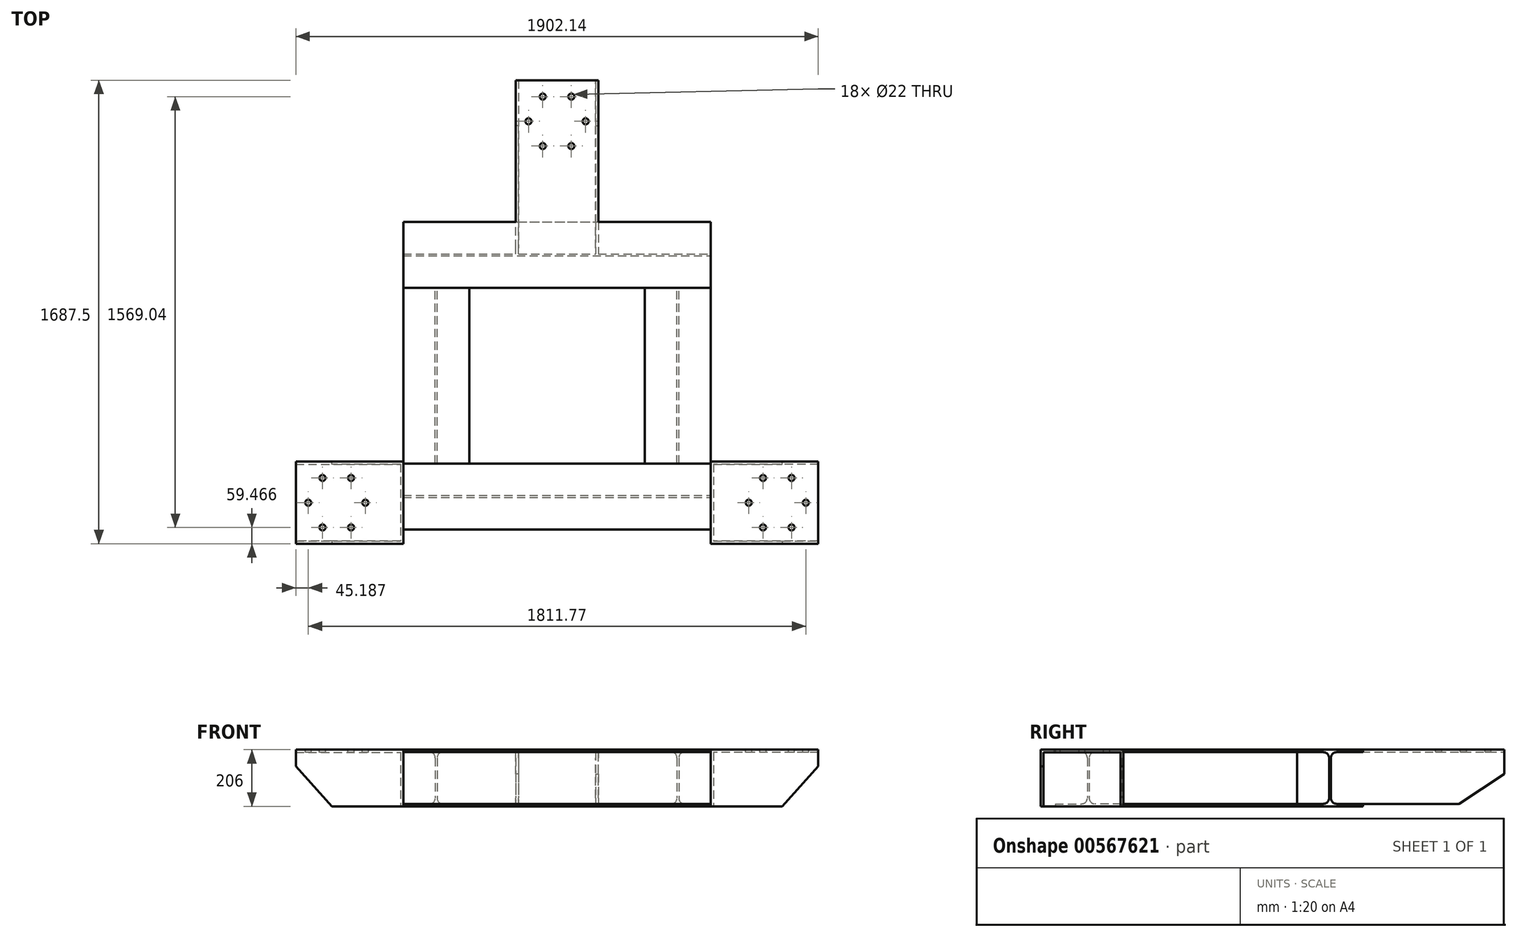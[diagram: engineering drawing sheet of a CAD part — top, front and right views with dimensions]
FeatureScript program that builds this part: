
annotation { "Feature Type Name" : "Feature", "Feature Type Description" : "" }
export const myFeature = defineFeature(function(context is Context, id is Id, definition is map)
    precondition{}
    {
        {
            var Q0;
            Q0=qCreatedBy(makeId("Top.planeOp"),FACE);
            var sketch = newSketch(context, id + "F0", { "sketchPlane" : qUnion([Q0])});
            skLineSegment(sketch, "E0.bottom", {"start": v(560, -560) * mm, "end": v(-560, -560) * mm});
            skLineSegment(sketch, "E0.top", {"start": v(560, 560) * mm, "end": v(-560, 560) * mm});
            skLineSegment(sketch, "E0.left", {"start": v(560, -560) * mm, "end": v(560, 560) * mm});
            skLineSegment(sketch, "E0.right", {"start": v(-560, -560) * mm, "end": v(-560, 560) * mm});
            skPoint(sketch, "E0.middle", {"position": v(0, 0) * mm});
            skSolve(sketch);
        }
        {
            var Q0;
            Q0=sQuery(id+"F0.wireOp",VERTEX,"E0.bottom.start");
            var Q1;
            Q1=sQuery(id+"F0.wireOp",EDGE,"E0.bottom");
            cPlane(context, id + "F1", {"entities" : qUnion([Q0, Q1]), "cplaneType" : CPlaneType.LINE_POINT, "offset" : 25 * mm, "width" : 150 * mm, "height" : 150 * mm});
        }
        {
            var Q0;
            Q0=qCreatedBy(id+"F1.planeOp",FACE);
            var sketch = newSketch(context, id + "F2", { "sketchPlane" : qUnion([Q0])});
            skLineSegment(sketch, "E1.bottom", {"start": v(560, 0) * mm, "end": v(320, 0) * mm});
            skLineSegment(sketch, "E1.top", {"start": v(560, -206) * mm, "end": v(320, -206) * mm});
            skLineSegment(sketch, "E1.left", {"start": v(560, 0) * mm, "end": v(560, -9) * mm});
            skLineSegment(sketch, "E1.right", {"start": v(320, 0) * mm, "end": v(320, -9) * mm});
            skLineSegment(sketch, "E2.bottom", {"start": v(560, -9) * mm, "end": v(464.25, -9) * mm});
            skLineSegment(sketch, "E2.top", {"start": v(560, -197) * mm, "end": v(464.25, -197) * mm});
            skLineSegment(sketch, "E2.right", {"start": v(443.25, -30) * mm, "end": v(443.25, -176) * mm});
            skLineSegment(sketch, "E3.bottom", {"start": v(320, -9) * mm, "end": v(415.75, -9) * mm});
            skLineSegment(sketch, "E3.top", {"start": v(320, -197) * mm, "end": v(415.75, -197) * mm});
            skLineSegment(sketch, "E3.right", {"start": v(436.75, -30) * mm, "end": v(436.75, -176) * mm});
            skLineSegment(sketch, "E4.trimOffspring", {"start": v(320, -197) * mm, "end": v(320, -206) * mm});
            skLineSegment(sketch, "E5.trimOffspring", {"start": v(560, -197) * mm, "end": v(560, -206) * mm});
            skPoint(sketch, "E6.visualSharp", {"position": v(443.25, -9) * mm});
            skArc(sketch, "E6.filletArc", {"start": v(464.25, -9) * mm, "mid": v(449.4, -15.15) * mm, "end": v(443.25, -30) * mm});
            skPoint(sketch, "E7.visualSharp", {"position": v(436.75, -9) * mm});
            skArc(sketch, "E7.filletArc", {"start": v(436.75, -30) * mm, "mid": v(430.6, -15.15) * mm, "end": v(415.75, -9) * mm});
            skPoint(sketch, "E8.visualSharp", {"position": v(436.75, -197) * mm});
            skArc(sketch, "E8.filletArc", {"start": v(415.75, -197) * mm, "mid": v(430.6, -190.85) * mm, "end": v(436.75, -176) * mm});
            skPoint(sketch, "E9.visualSharp", {"position": v(443.25, -197) * mm});
            skArc(sketch, "E9.filletArc", {"start": v(443.25, -176) * mm, "mid": v(449.4, -190.85) * mm, "end": v(464.25, -197) * mm});
            skLineSegment(sketch, "E10", {"start": v(0, 0) * mm, "end": v(0, -326.36) * mm});
            skLineSegment(sketch, "E11.MirrorCS", {"start": v(-560, 0) * mm, "end": v(-560, -9) * mm});
            skArc(sketch, "E12.MirrorCS", {"start": v(-464.25, -9) * mm, "mid": v(-449.4, -15.15) * mm, "end": v(-443.25, -30) * mm});
            skArc(sketch, "E13.MirrorCS", {"start": v(-415.75, -197) * mm, "mid": v(-430.6, -190.85) * mm, "end": v(-436.75, -176) * mm});
            skArc(sketch, "E14.MirrorCS", {"start": v(-443.25, -176) * mm, "mid": v(-449.4, -190.85) * mm, "end": v(-464.25, -197) * mm});
            skLineSegment(sketch, "E15.MirrorCS", {"start": v(-320, -197) * mm, "end": v(-320, -206) * mm});
            skArc(sketch, "E16.MirrorCS", {"start": v(-436.75, -30) * mm, "mid": v(-430.6, -15.15) * mm, "end": v(-415.75, -9) * mm});
            skLineSegment(sketch, "E17.MirrorCS", {"start": v(-560, -197) * mm, "end": v(-560, -206) * mm});
            skLineSegment(sketch, "E18.MirrorCS", {"start": v(-320, 0) * mm, "end": v(-320, -9) * mm});
            skLineSegment(sketch, "E19.MirrorCS", {"start": v(-320, -197) * mm, "end": v(-415.75, -197) * mm});
            skLineSegment(sketch, "E20.MirrorCS", {"start": v(-320, -9) * mm, "end": v(-415.75, -9) * mm});
            skLineSegment(sketch, "E21.MirrorCS", {"start": v(-443.25, -30) * mm, "end": v(-443.25, -176) * mm});
            skPoint(sketch, "E22.MirrorP", {"position": v(-436.75, -197) * mm});
            skLineSegment(sketch, "E23.MirrorCS", {"start": v(-560, 0) * mm, "end": v(-320, 0) * mm});
            skPoint(sketch, "E24.MirrorP", {"position": v(-443.25, -197) * mm});
            skPoint(sketch, "E25.MirrorP", {"position": v(-436.75, -9) * mm});
            skLineSegment(sketch, "E26.MirrorCS", {"start": v(-560, -206) * mm, "end": v(-320, -206) * mm});
            skPoint(sketch, "E27.MirrorP", {"position": v(-443.25, -9) * mm});
            skLineSegment(sketch, "E28.MirrorCS", {"start": v(-560, -9) * mm, "end": v(-464.25, -9) * mm});
            skLineSegment(sketch, "E29.MirrorCS", {"start": v(-560, -197) * mm, "end": v(-464.25, -197) * mm});
            skLineSegment(sketch, "E30.MirrorCS", {"start": v(-436.75, -30) * mm, "end": v(-436.75, -176) * mm});
            skSolve(sketch);
        }
        {
            var Q0;
            Q0 = qSketchRegion(id + "F2", true);
            extrude(context, id + "F3", {"entities" : qUnion([Q0]), "depth" : 1120 * mm, "offsetDistance" : 25 * mm});
        }
        {
            var Q0;
            Q0=makeQuery(id+"F3.opExtrude","SWEPT_FACE",FACE,{"disambiguationData":[OSD([sQuery(id+"F2.wireOp",EDGE,"E18.MirrorCS")])]});
            var sketch = newSketch(context, id + "F4", { "sketchPlane" : qUnion([Q0])});
            skLineSegment(sketch, "E31.MirrorCS", {"start": v(-560, 0) * mm, "end": v(-560, -9) * mm});
            skArc(sketch, "E32.MirrorCS", {"start": v(-464.25, -9) * mm, "mid": v(-449.4, -15.15) * mm, "end": v(-443.25, -30) * mm});
            skArc(sketch, "E33.MirrorCS", {"start": v(-415.75, -197) * mm, "mid": v(-430.6, -190.85) * mm, "end": v(-436.75, -176) * mm});
            skArc(sketch, "E34.MirrorCS", {"start": v(-443.25, -176) * mm, "mid": v(-449.4, -190.85) * mm, "end": v(-464.25, -197) * mm});
            skLineSegment(sketch, "E35.MirrorCS", {"start": v(-320, -197) * mm, "end": v(-320, -206) * mm});
            skArc(sketch, "E36.MirrorCS", {"start": v(-436.75, -30) * mm, "mid": v(-430.6, -15.15) * mm, "end": v(-415.75, -9) * mm});
            skLineSegment(sketch, "E37.MirrorCS", {"start": v(-560, -197) * mm, "end": v(-560, -206) * mm});
            skLineSegment(sketch, "E38.MirrorCS", {"start": v(-320, 0) * mm, "end": v(-320, -9) * mm});
            skLineSegment(sketch, "E39.MirrorCS", {"start": v(-320, -197) * mm, "end": v(-415.75, -197) * mm});
            skLineSegment(sketch, "E40.MirrorCS", {"start": v(-320, -9) * mm, "end": v(-415.75, -9) * mm});
            skLineSegment(sketch, "E41.MirrorCS", {"start": v(-443.25, -30) * mm, "end": v(-443.25, -176) * mm});
            skPoint(sketch, "E42.MirrorP", {"position": v(-436.75, -197) * mm});
            skLineSegment(sketch, "E43.MirrorCS", {"start": v(-560, 0) * mm, "end": v(-320, 0) * mm});
            skPoint(sketch, "E44.MirrorP", {"position": v(-443.25, -197) * mm});
            skPoint(sketch, "E45.MirrorP", {"position": v(-436.75, -9) * mm});
            skLineSegment(sketch, "E46.MirrorCS", {"start": v(-560, -206) * mm, "end": v(-320, -206) * mm});
            skPoint(sketch, "E47.MirrorP", {"position": v(-443.25, -9) * mm});
            skLineSegment(sketch, "E48.MirrorCS", {"start": v(-560, -9) * mm, "end": v(-464.25, -9) * mm});
            skLineSegment(sketch, "E49.MirrorCS", {"start": v(-560, -197) * mm, "end": v(-464.25, -197) * mm});
            skLineSegment(sketch, "E50.MirrorCS", {"start": v(-436.75, -30) * mm, "end": v(-436.75, -176) * mm});
            skPoint(sketch, "E51.endSnap0", {"position": v(0, -9) * mm});
            skLineSegment(sketch, "E52.MirrorCS", {"start": v(560, -197) * mm, "end": v(560, -206) * mm});
            skArc(sketch, "E53.MirrorCS", {"start": v(415.75, -197) * mm, "mid": v(430.6, -190.85) * mm, "end": v(436.75, -176) * mm});
            skLineSegment(sketch, "E54.MirrorCS", {"start": v(560, 0) * mm, "end": v(560, -9) * mm});
            skArc(sketch, "E55.MirrorCS", {"start": v(443.25, -176) * mm, "mid": v(449.4, -190.85) * mm, "end": v(464.25, -197) * mm});
            skArc(sketch, "E56.MirrorCS", {"start": v(436.75, -30) * mm, "mid": v(430.6, -15.15) * mm, "end": v(415.75, -9) * mm});
            skArc(sketch, "E57.MirrorCS", {"start": v(464.25, -9) * mm, "mid": v(449.4, -15.15) * mm, "end": v(443.25, -30) * mm});
            skLineSegment(sketch, "E58.MirrorCS", {"start": v(320, -197) * mm, "end": v(320, -206) * mm});
            skPoint(sketch, "E59.MirrorP", {"position": v(436.75, -9) * mm});
            skLineSegment(sketch, "E60.MirrorCS", {"start": v(320, -197) * mm, "end": v(415.75, -197) * mm});
            skLineSegment(sketch, "E61.MirrorCS", {"start": v(443.25, -30) * mm, "end": v(443.25, -176) * mm});
            skLineSegment(sketch, "E62.MirrorCS", {"start": v(560, -197) * mm, "end": v(464.25, -197) * mm});
            skLineSegment(sketch, "E63.MirrorCS", {"start": v(560, -9) * mm, "end": v(464.25, -9) * mm});
            skLineSegment(sketch, "E64.MirrorCS", {"start": v(436.75, -30) * mm, "end": v(436.75, -176) * mm});
            skLineSegment(sketch, "E65.MirrorCS", {"start": v(560, -206) * mm, "end": v(320, -206) * mm});
            skPoint(sketch, "E66.MirrorP", {"position": v(443.25, -9) * mm});
            skPoint(sketch, "E67.MirrorP", {"position": v(443.25, -197) * mm});
            skPoint(sketch, "E68.MirrorP", {"position": v(436.75, -197) * mm});
            skLineSegment(sketch, "E69.MirrorCS", {"start": v(320, -9) * mm, "end": v(415.75, -9) * mm});
            skLineSegment(sketch, "E70.MirrorCS", {"start": v(560, 0) * mm, "end": v(320, 0) * mm});
            skLineSegment(sketch, "E71", {"start": v(320, 0) * mm, "end": v(320, -9) * mm});
            skSolve(sketch);
        }
        {
            var Q0;
            Q0 = qSketchRegion(id + "F4", true);
            var Q1;
            Q1=makeQuery(id+"F3.opExtrude","SWEPT_FACE",FACE,{"disambiguationData":[OSD([sQuery(id+"F2.wireOp",EDGE,"E4.trimOffspring")])]});
            extrude(context, id + "F5", {"entities" : qUnion([Q0]), "endBound" : BoundingType.UP_TO_SURFACE, "depth" : 25 * mm, "endBoundEntityFace" : qUnion([Q1]), "offsetDistance" : 25 * mm});
        }
        {
            var Q0;
            Q0=makeQuery(id+"F0.imprint","IMPRINT",FACE,{"disambiguationData":[TD([[makeQuery(id+"F0.imprint","IMPRINT",EDGE,{"derivedFrom":sQuery(id+"F0.wireOp",EDGE,"E0.bottom")}),-1.0]])]});
            var sketch = newSketch(context, id + "F6", { "sketchPlane" : qUnion([Q0])});
            skLineSegment(sketch, "E72", {"start": v(-801.07, -462.5) * mm, "end": v(801.07, -462.5) * mm});
            skLineSegment(sketch, "E73", {"start": v(0, 925) * mm, "end": v(-801.07, -462.5) * mm});
            skLineSegment(sketch, "E74", {"start": v(0, 925) * mm, "end": v(801.07, -462.5) * mm});
            skLineSegment(sketch, "E75", {"start": v(-801.07, -462.5) * mm, "end": v(400.54, 231.25) * mm});
            skLineSegment(sketch, "E76", {"start": v(801.07, -462.5) * mm, "end": v(-400.54, 231.25) * mm});
            skPoint(sketch, "E77", {"position": v(0, 0) * mm});
            skSolve(sketch);
        }
        {
            var Q0;
            Q0=makeQuery(id+"F0.imprint","IMPRINT",FACE,{"disambiguationData":[TD([[makeQuery(id+"F0.imprint","IMPRINT",EDGE,{"derivedFrom":sQuery(id+"F0.wireOp",EDGE,"E0.bottom")}),-1.0]])]});
            var sketch = newSketch(context, id + "F7", { "sketchPlane" : qUnion([Q0])});
            skLineSegment(sketch, "E78.0", {"start": v(560, 560) * mm, "end": v(-560, 560) * mm, "construction": true});
            skLineSegment(sketch, "E79.bottom", {"start": v(-150, 560) * mm, "end": v(150, 560) * mm});
            skLineSegment(sketch, "E79.left", {"start": v(-150, 560) * mm, "end": v(-150, 925) * mm});
            skLineSegment(sketch, "E79.right", {"start": v(150, 560) * mm, "end": v(150, 925) * mm});
            skLineSegment(sketch, "E80", {"start": v(-150, 925) * mm, "end": v(-150, 1075) * mm});
            skLineSegment(sketch, "E81", {"start": v(-150, 1075) * mm, "end": v(150, 1075) * mm});
            skLineSegment(sketch, "E82", {"start": v(150, 925) * mm, "end": v(150, 1075) * mm});
            skSolve(sketch);
        }
        {
            var Q0;
            Q0=makeQuery(id+"F7.imprint","IMPRINT",FACE,{"disambiguationData":[TD([[makeQuery(id+"F7.imprint","IMPRINT",EDGE,{"derivedFrom":sQuery(id+"F7.wireOp",EDGE,"E79.bottom")}),-1.0]])]});
            extrude(context, id + "F8", {"entities" : qUnion([Q0]), "operationType" : NewBodyOperationType.ADD, "oppositeDirection" : true, "depth" : 9 * mm, "offsetDistance" : 25 * mm});
        }
        {
            var Q0;
            Q0=makeQuery(id+"F8.opExtrude","SWEPT_FACE",FACE,{"disambiguationData":[OSD([sQuery(id+"F7.wireOp",EDGE,"E79.left"),sQuery(id+"F7.wireOp",EDGE,"E80")])]});
            var sketch = newSketch(context, id + "F9", { "sketchPlane" : qUnion([Q0])});
            skLineSegment(sketch, "E83.0", {"start": v(-560, -9) * mm, "end": v(-464.25, -9) * mm});
            skArc(sketch, "E84.0", {"start": v(-464.25, -9) * mm, "mid": v(-449.4, -15.15) * mm, "end": v(-443.25, -30) * mm});
            skLineSegment(sketch, "E85.0", {"start": v(-443.25, -30) * mm, "end": v(-443.25, -176) * mm});
            skArc(sketch, "E86.0", {"start": v(-443.25, -176) * mm, "mid": v(-449.4, -190.85) * mm, "end": v(-464.25, -197) * mm});
            skLineSegment(sketch, "E87.0", {"start": v(-560, -197) * mm, "end": v(-464.25, -197) * mm});
            skLineSegment(sketch, "E88.0", {"start": v(-560, -9) * mm, "end": v(-560, -9) * mm});
            skLineSegment(sketch, "E89", {"start": v(-560, -197) * mm, "end": v(747.25, -197) * mm});
            skLineSegment(sketch, "E90", {"start": v(-560, -197) * mm, "end": v(-910, -197) * mm});
            skLineSegment(sketch, "E91", {"start": v(-1075, -9) * mm, "end": v(-1075, -89) * mm});
            skLineSegment(sketch, "E92", {"start": v(-1075, -89) * mm, "end": v(-910, -197) * mm});
            skLineSegment(sketch, "E93", {"start": v(-560, -9) * mm, "end": v(-1075, -9) * mm});
            skSolve(sketch);
        }
        {
            var Q0;
            Q0=makeQuery(id+"F9.imprint","IMPRINT",FACE,{"disambiguationData":[TD([[makeQuery(id+"F9.imprint","IMPRINT",EDGE,{"derivedFrom":sQuery(id+"F9.wireOp",EDGE,"E83.0")}),-1.0]])]});
            extrude(context, id + "F10", {"entities" : qUnion([Q0]), "operationType" : NewBodyOperationType.ADD, "oppositeDirection" : true, "depth" : 10 * mm, "offsetDistance" : 25 * mm});
        }
        {
            var Q0;
            Q0=makeQuery(id+"F8.opExtrude","SWEPT_FACE",FACE,{"disambiguationData":[OSD([sQuery(id+"F7.wireOp",EDGE,"E79.right"),sQuery(id+"F7.wireOp",EDGE,"E82")])]});
            var sketch = newSketch(context, id + "F11", { "sketchPlane" : qUnion([Q0])});
            skLineSegment(sketch, "E94.0.0", {"start": v(560, 0) * mm, "end": v(1075, 0) * mm});
            skLineSegment(sketch, "E94.0.1", {"start": v(1075, 0) * mm, "end": v(1075, -89) * mm});
            skLineSegment(sketch, "E94.0.2", {"start": v(1075, -89) * mm, "end": v(910, -197) * mm});
            skLineSegment(sketch, "E94.0.3", {"start": v(910, -197) * mm, "end": v(560, -197) * mm});
            skLineSegment(sketch, "E94.0.4", {"start": v(560, -197) * mm, "end": v(464.25, -197) * mm});
            skArc(sketch, "E94.0.5", {"start": v(464.25, -197) * mm, "mid": v(449.4, -190.85) * mm, "end": v(443.25, -176) * mm});
            skLineSegment(sketch, "E94.0.6", {"start": v(443.25, -176) * mm, "end": v(443.25, -30) * mm});
            skArc(sketch, "E94.0.7", {"start": v(443.25, -30) * mm, "mid": v(449.4, -15.15) * mm, "end": v(464.25, -9) * mm});
            skLineSegment(sketch, "E94.0.8", {"start": v(464.25, -9) * mm, "end": v(560, -9) * mm});
            skLineSegment(sketch, "E94.0.9", {"start": v(560, -9) * mm, "end": v(560, 0) * mm});
            skSolve(sketch);
        }
        {
            var Q0;
            {var subQ0=sQuery(id+"F11.wireOp",EDGE,"E94.0.2");Q0=makeQuery(id+"F11.imprint","IMPRINT",FACE,{"disambiguationData":[TD([[makeQuery(id+"F11.imprint","IMPRINT",EDGE,{"derivedFrom":subQ0}),-1.0]])]});}
            extrude(context, id + "F12", {"entities" : qUnion([Q0]), "operationType" : NewBodyOperationType.ADD, "oppositeDirection" : true, "depth" : 10 * mm, "offsetDistance" : 25 * mm});
        }
        {
            var Q0;
            Q0=makeQuery(id+"F3.opExtrude","CAP_FACE",FACE,{"disambiguationData":[OSD([sQuery(id+"F2.wireOp",EDGE,"E1.bottom"),sQuery(id+"F2.wireOp",EDGE,"E1.top"),sQuery(id+"F2.wireOp",EDGE,"E1.left"),sQuery(id+"F2.wireOp",EDGE,"E1.right"),sQuery(id+"F2.wireOp",EDGE,"E2.bottom"),sQuery(id+"F2.wireOp",EDGE,"E2.top"),sQuery(id+"F2.wireOp",EDGE,"E2.right"),sQuery(id+"F2.wireOp",EDGE,"E3.bottom"),sQuery(id+"F2.wireOp",EDGE,"E3.top"),sQuery(id+"F2.wireOp",EDGE,"E3.right"),sQuery(id+"F2.wireOp",EDGE,"E4.trimOffspring"),sQuery(id+"F2.wireOp",EDGE,"E5.trimOffspring"),sQuery(id+"F2.wireOp",EDGE,"E6.filletArc"),sQuery(id+"F2.wireOp",EDGE,"E7.filletArc"),sQuery(id+"F2.wireOp",EDGE,"E8.filletArc"),sQuery(id+"F2.wireOp",EDGE,"E9.filletArc")])],"isStart":false});
            var sketch = newSketch(context, id + "F13", { "sketchPlane" : qUnion([Q0])});
            skLineSegment(sketch, "E95.top", {"start": v(312.5, -206) * mm, "end": v(560, -206) * mm});
            skPoint(sketch, "E96.0", {"position": v(462.5, 0) * mm});
            skLineSegment(sketch, "E97", {"start": v(462.5, 0) * mm, "end": v(612.5, 0) * mm});
            skLineSegment(sketch, "E98", {"start": v(462.5, 0) * mm, "end": v(312.5, 0) * mm});
            skLineSegment(sketch, "E99", {"start": v(312.5, 0) * mm, "end": v(312.5, -206) * mm});
            skLineSegment(sketch, "E100", {"start": v(312.5, -206) * mm, "end": v(612.5, -206) * mm});
            skLineSegment(sketch, "E101", {"start": v(612.5, 0) * mm, "end": v(612.5, -206) * mm});
            skSolve(sketch);
        }
        {
            var Q0;
            {var subQ3=sQuery(id+"F13.wireOp",EDGE,"E99");Q0=makeQuery(id+"F13.imprint","IMPRINT",FACE,{"disambiguationData":[TD([[makeQuery(id+"F13.imprint","IMPRINT",EDGE,{"derivedFrom":subQ3}),1.0]])]});}
            var Q1;
            {var subQ2=makeQuery(id+"F3.opExtrude","CAP_EDGE",EDGE,{"disambiguationData":[OSD([sQuery(id+"F2.wireOp",EDGE,"E1.left")])],"isStart":false});Q1=makeQuery(id+"F13.imprint","IMPRINT",FACE,{"disambiguationData":[TD([[makeQuery(id+"F13.imprint","IMPRINT",EDGE,{"derivedFrom":subQ2}),-1.0]])]});}
            var Q2;
            {var subQ1=sQuery(id+"F13.wireOp",EDGE,"E101");Q2=makeQuery(id+"F13.imprint","IMPRINT",FACE,{"disambiguationData":[TD([[makeQuery(id+"F13.imprint","IMPRINT",EDGE,{"derivedFrom":subQ1}),-1.0]])]});}
            extrude(context, id + "F14", {"entities" : qUnion([Q0, Q1, Q2]), "depth" : 10 * mm, "offsetDistance" : 25 * mm});
        }
        {
            var Q0;
            Q0=makeQuery(id+"F14.opExtrude","CAP_FACE",FACE,{"disambiguationData":[OSD([sQuery(id+"F13.wireOp",EDGE,"E97"),sQuery(id+"F13.wireOp",EDGE,"E98"),sQuery(id+"F13.wireOp",EDGE,"E99"),sQuery(id+"F13.wireOp",EDGE,"E100"),sQuery(id+"F13.wireOp",EDGE,"E101")])],"isStart":false});
            var sketch = newSketch(context, id + "F15", { "sketchPlane" : qUnion([Q0])});
            skLineSegment(sketch, "E102.bottom", {"start": v(312.5, 0) * mm, "end": v(612.5, 0) * mm});
            skLineSegment(sketch, "E102.top", {"start": v(312.5, -10) * mm, "end": v(612.5, -10) * mm});
            skLineSegment(sketch, "E102.left", {"start": v(312.5, 0) * mm, "end": v(312.5, -10) * mm});
            skLineSegment(sketch, "E102.right", {"start": v(612.5, 0) * mm, "end": v(612.5, -10) * mm});
            skSolve(sketch);
        }
        {
            var Q0;
            Q0=makeQuery(id+"F15.imprint","IMPRINT",FACE,{"disambiguationData":[TD([[makeQuery(id+"F15.imprint","IMPRINT",EDGE,{"derivedFrom":sQuery(id+"F15.wireOp",EDGE,"E102.bottom")}),1.0]])]});
            extrude(context, id + "F16", {"entities" : qUnion([Q0]), "operationType" : NewBodyOperationType.ADD, "depth" : 381.07 * mm, "offsetDistance" : 25 * mm});
        }
        {
            var Q0;
            Q0=makeQuery(id+"F16.boolean.opBoolean","MERGE",FACE,{"derivedFrom":[makeQuery(id+"F14.opExtrude","SWEPT_FACE",FACE,{"disambiguationData":[OSD([sQuery(id+"F13.wireOp",EDGE,"E99")])]}),makeQuery(id+"F16.opExtrude","SWEPT_FACE",FACE,{"disambiguationData":[OSD([sQuery(id+"F15.wireOp",EDGE,"E102.left")])]})]});
            var sketch = newSketch(context, id + "F17", { "sketchPlane" : qUnion([Q0])});
            skLineSegment(sketch, "E103", {"start": v(951.07, -10) * mm, "end": v(951.07, -60) * mm});
            skLineSegment(sketch, "E104", {"start": v(570, -206) * mm, "end": v(820, -206) * mm});
            skLineSegment(sketch, "E105", {"start": v(951.07, -60) * mm, "end": v(820, -206) * mm});
            skSolve(sketch);
        }
        {
            var Q0;
            Q0=makeQuery(id+"F17.imprint","IMPRINT",FACE,{"disambiguationData":[TD([[makeQuery(id+"F17.imprint","IMPRINT",EDGE,{"derivedFrom":sQuery(id+"F17.wireOp",EDGE,"E103")}),-1.0]])]});
            extrude(context, id + "F18", {"entities" : qUnion([Q0]), "operationType" : NewBodyOperationType.ADD, "oppositeDirection" : true, "depth" : 10 * mm, "offsetDistance" : 25 * mm});
        }
        {
            var Q0;
            Q0=makeQuery(id+"F16.boolean.opBoolean","MERGE",FACE,{"derivedFrom":[makeQuery(id+"F14.opExtrude","SWEPT_FACE",FACE,{"disambiguationData":[OSD([sQuery(id+"F13.wireOp",EDGE,"E101")])]}),makeQuery(id+"F16.opExtrude","SWEPT_FACE",FACE,{"disambiguationData":[OSD([sQuery(id+"F15.wireOp",EDGE,"E102.right")])]})]});
            var sketch = newSketch(context, id + "F19", { "sketchPlane" : qUnion([Q0])});
            skLineSegment(sketch, "E106.0.0", {"start": v(-560, -206) * mm, "end": v(-820, -206) * mm});
            skLineSegment(sketch, "E106.0.1", {"start": v(-820, -206) * mm, "end": v(-951.07, -60) * mm});
            skLineSegment(sketch, "E106.0.2", {"start": v(-951.07, -60) * mm, "end": v(-951.07, 0) * mm});
            skLineSegment(sketch, "E106.0.3", {"start": v(-951.07, 0) * mm, "end": v(-560, 0) * mm});
            skLineSegment(sketch, "E106.0.4", {"start": v(-560, 0) * mm, "end": v(-560, -206) * mm});
            skSolve(sketch);
        }
        {
            var Q0;
            {var subQ3=sQuery(id+"F19.wireOp",EDGE,"E106.0.1");Q0=makeQuery(id+"F19.imprint","IMPRINT",FACE,{"disambiguationData":[TD([[makeQuery(id+"F19.imprint","IMPRINT",EDGE,{"derivedFrom":subQ3}),-1.0]])]});}
            extrude(context, id + "F20", {"entities" : qUnion([Q0]), "operationType" : NewBodyOperationType.ADD, "oppositeDirection" : true, "depth" : 10 * mm, "offsetDistance" : 25 * mm});
        }
        {
            var Q0;
            Q0=makeQuery(id+"F14.opExtrude","SWEPT_BODY",BODY,{"disambiguationData":[OSD([sQuery(id+"F13.wireOp",EDGE,"E97"),sQuery(id+"F13.wireOp",EDGE,"E98"),sQuery(id+"F13.wireOp",EDGE,"E99"),sQuery(id+"F13.wireOp",EDGE,"E100"),sQuery(id+"F13.wireOp",EDGE,"E101")])]});
            var Q1;
            Q1=qCreatedBy(makeId("Right.planeOp"),FACE);
            mirror(context, id + "F21", {"entities" : qUnion([Q0]), "mirrorPlane" : qUnion([Q1])});
        }
        {
            var Q0;
            Q0=makeQuery(id+"F8.boolean.opBoolean","MERGE",FACE,{"derivedFrom":[makeQuery(id+"F3.opExtrude","SWEPT_FACE",FACE,{"disambiguationData":[OSD([sQuery(id+"F2.wireOp",EDGE,"E23.MirrorCS")])]}),makeQuery(id+"F8.opExtrude","CAP_FACE",FACE,{"disambiguationData":[OSD([sQuery(id+"F7.wireOp",EDGE,"E79.bottom"),sQuery(id+"F7.wireOp",EDGE,"E79.left"),sQuery(id+"F7.wireOp",EDGE,"E79.right"),sQuery(id+"F7.wireOp",EDGE,"E80"),sQuery(id+"F7.wireOp",EDGE,"E81"),sQuery(id+"F7.wireOp",EDGE,"E82")])],"isStart":true})]});
            var sketch = newSketch(context, id + "F22", { "sketchPlane" : qUnion([Q0])});
            skLineSegment(sketch, "E107", {"start": v(104, 925.93) * mm, "end": v(150, 925.93) * mm, "construction": true});
            skCircle(sketch, "E108", {"center": v(104, 925.93) * mm, "radius": 11 * mm});
            skPoint(sketch, "E109.center", {"position": v(0, 0) * mm});
            skPoint(sketch, "E110", {"position": v(0, 925.93) * mm});
            skCircle(sketch, "E111.1.0", {"center": v(-853.88, -372.9) * mm, "radius": 11 * mm});
            skCircle(sketch, "E111.2.0", {"center": v(749.88, -553.03) * mm, "radius": 11 * mm});
            skCircle(sketch, "E112", {"center": v(0, 925.93) * mm, "radius": 104 * mm, "construction": true});
            skLineSegment(sketch, "E113", {"start": v(0, 925.93) * mm, "end": v(0, 954.37) * mm, "construction": true});
            skCircle(sketch, "E114.MirrorC", {"center": v(-104, 925.93) * mm, "radius": 11 * mm});
            skLineSegment(sketch, "E115", {"start": v(0, 925.93) * mm, "end": v(-104, 925.93) * mm, "construction": true});
            skLineSegment(sketch, "E116", {"start": v(0, 925.93) * mm, "end": v(-52, 1016) * mm, "construction": true});
            skCircle(sketch, "E117", {"center": v(-52, 1016) * mm, "radius": 11 * mm});
            skLineSegment(sketch, "E118", {"start": v(0, 925.93) * mm, "end": v(-52, 835.87) * mm, "construction": true});
            skCircle(sketch, "E119", {"center": v(-52, 835.87) * mm, "radius": 11 * mm});
            skCircle(sketch, "E120.MirrorC", {"center": v(52, 1016) * mm, "radius": 11 * mm});
            skCircle(sketch, "E121.MirrorC", {"center": v(52, 835.87) * mm, "radius": 11 * mm});
            skPoint(sketch, "E122.1.0", {"position": v(-801.88, -462.97) * mm});
            skCircle(sketch, "E122.1.1", {"center": v(-905.88, -462.97) * mm, "radius": 11 * mm});
            skCircle(sketch, "E122.1.2", {"center": v(-801.88, -462.97) * mm, "radius": 104 * mm, "construction": true});
            skCircle(sketch, "E122.1.3", {"center": v(-697.88, -462.97) * mm, "radius": 11 * mm});
            skLineSegment(sketch, "E122.1.4", {"start": v(-801.88, -462.97) * mm, "end": v(-697.88, -462.97) * mm, "construction": true});
            skCircle(sketch, "E122.1.5", {"center": v(-853.88, -553.03) * mm, "radius": 11 * mm});
            skLineSegment(sketch, "E122.1.6", {"start": v(-801.88, -462.97) * mm, "end": v(-853.88, -553.03) * mm, "construction": true});
            skLineSegment(sketch, "E122.1.7", {"start": v(-801.88, -462.97) * mm, "end": v(-749.88, -553.03) * mm, "construction": true});
            skCircle(sketch, "E122.1.8", {"center": v(-749.88, -553.03) * mm, "radius": 11 * mm});
            skCircle(sketch, "E122.1.9", {"center": v(-749.88, -372.9) * mm, "radius": 11 * mm});
            skLineSegment(sketch, "E122.1.10", {"start": v(-853.88, -372.9) * mm, "end": v(-876.88, -333.06) * mm, "construction": true});
            skLineSegment(sketch, "E122.1.12", {"start": v(-801.88, -462.97) * mm, "end": v(-826.5, -477.18) * mm, "construction": true});
            skPoint(sketch, "E122.2.0", {"position": v(801.88, -462.97) * mm});
            skCircle(sketch, "E122.2.1", {"center": v(853.88, -553.03) * mm, "radius": 11 * mm});
            skCircle(sketch, "E122.2.2", {"center": v(801.88, -462.97) * mm, "radius": 104 * mm, "construction": true});
            skCircle(sketch, "E122.2.3", {"center": v(749.88, -372.9) * mm, "radius": 11 * mm});
            skLineSegment(sketch, "E122.2.4", {"start": v(801.88, -462.97) * mm, "end": v(749.88, -372.9) * mm, "construction": true});
            skCircle(sketch, "E122.2.5", {"center": v(905.88, -462.97) * mm, "radius": 11 * mm});
            skLineSegment(sketch, "E122.2.6", {"start": v(801.88, -462.97) * mm, "end": v(905.88, -462.97) * mm, "construction": true});
            skLineSegment(sketch, "E122.2.7", {"start": v(801.88, -462.97) * mm, "end": v(853.88, -372.9) * mm, "construction": true});
            skCircle(sketch, "E122.2.8", {"center": v(853.88, -372.9) * mm, "radius": 11 * mm});
            skCircle(sketch, "E122.2.9", {"center": v(697.88, -462.97) * mm, "radius": 11 * mm});
            skLineSegment(sketch, "E122.2.10", {"start": v(749.88, -553.03) * mm, "end": v(726.88, -592.87) * mm, "construction": true});
            skLineSegment(sketch, "E122.2.12", {"start": v(801.88, -462.97) * mm, "end": v(826.5, -477.18) * mm, "construction": true});
            skSolve(sketch);
        }
        {
            var Q0;
            Q0 = qSketchRegion(id + "F22", true);
            extrude(context, id + "F23", {"entities" : qUnion([Q0]), "operationType" : NewBodyOperationType.REMOVE, "oppositeDirection" : true, "depth" : 25 * mm, "offsetDistance" : 25 * mm});
        }
    });
